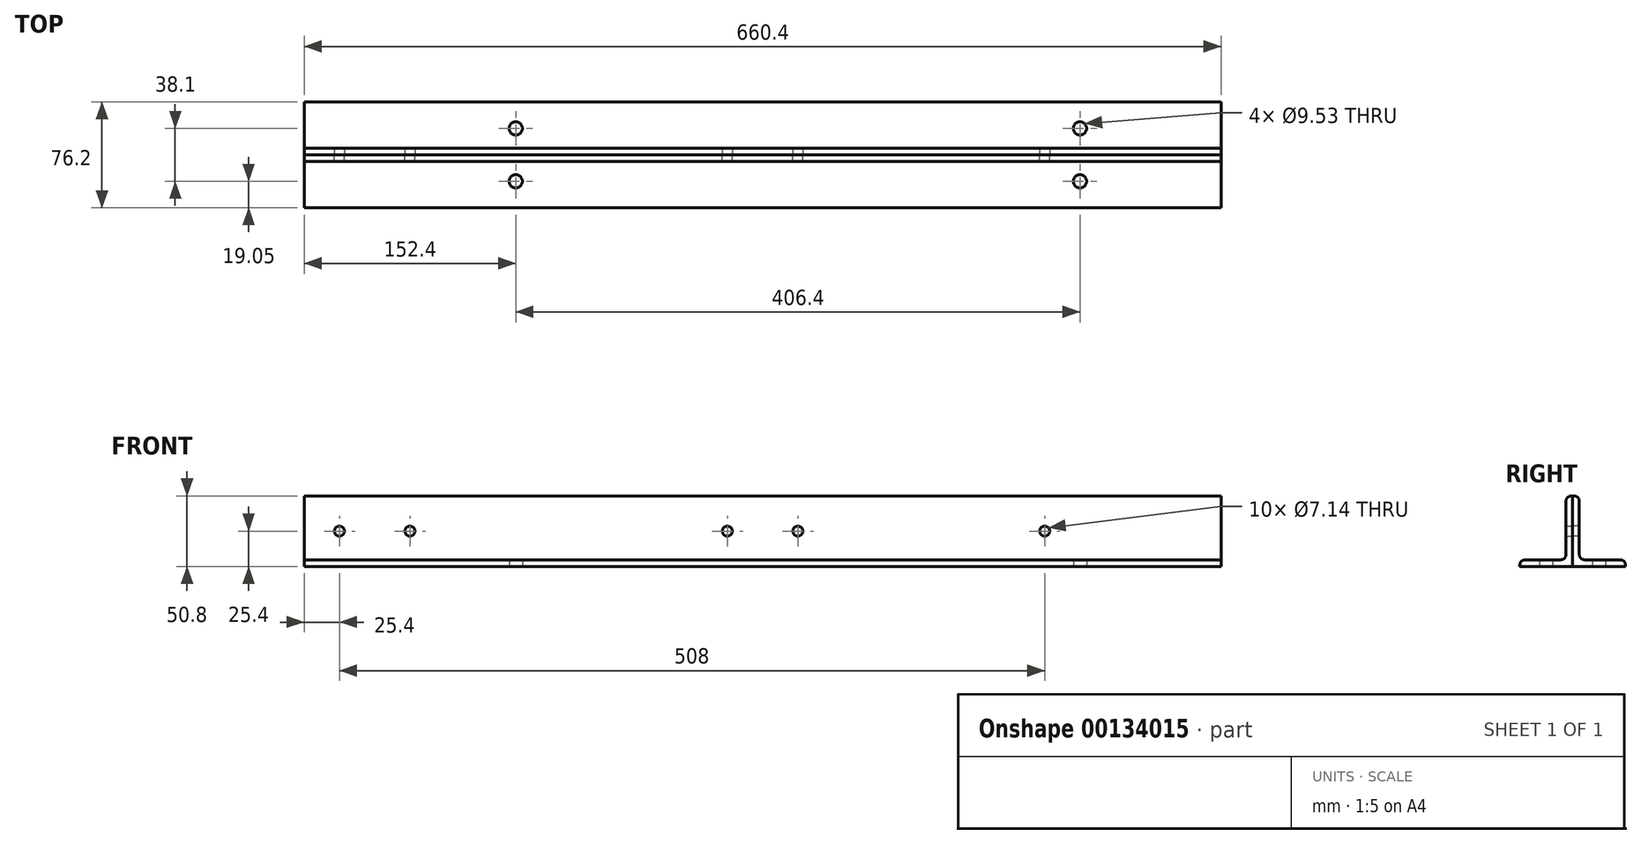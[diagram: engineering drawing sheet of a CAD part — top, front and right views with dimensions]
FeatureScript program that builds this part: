
annotation { "Feature Type Name" : "Feature", "Feature Type Description" : "" }
export const myFeature = defineFeature(function(context is Context, id is Id, definition is map)
    precondition{}
    {
        {
            var Q0;
            Q0=qCreatedBy(makeId("Right.planeOp"),FACE);
            var sketch = newSketch(context, id + "F0", { "sketchPlane" : qUnion([Q0])});
            skLineSegment(sketch, "E0", {"start": v(0, 50.8) * mm, "end": v(0, 0) * mm});
            skLineSegment(sketch, "E1", {"start": v(0, 0) * mm, "end": v(-38.1, 0) * mm});
            skLineSegment(sketch, "E2", {"start": v(0, 50.8) * mm, "end": v(-0.97, 50.8) * mm});
            skLineSegment(sketch, "E3", {"start": v(-38.1, 0) * mm, "end": v(-38.1, 0.95) * mm});
            skLineSegment(sketch, "E4", {"start": v(-34.3, 4.76) * mm, "end": v(-8.59, 4.76) * mm});
            skLineSegment(sketch, "E5", {"start": v(-4.78, 47) * mm, "end": v(-4.78, 8.57) * mm});
            skArc(sketch, "E6", {"start": v(-38.1, 0.95) * mm, "mid": v(-36.98, 3.65) * mm, "end": v(-34.3, 4.76) * mm});
            skArc(sketch, "E7", {"start": v(-8.59, 4.76) * mm, "mid": v(-5.9, 5.88) * mm, "end": v(-4.78, 8.57) * mm});
            skArc(sketch, "E8", {"start": v(-4.78, 47) * mm, "mid": v(-3.66, 49.68) * mm, "end": v(-0.97, 50.8) * mm});
            skPoint(sketch, "E9.endSnap0", {"position": v(0, 25.4) * mm});
            skSolve(sketch);
        }
        {
            var Q0;
            Q0 = qSketchRegion(id + "F0", true);
            extrude(context, id + "F1", {"entities" : qUnion([Q0]), "endBound" : BoundingType.SYMMETRIC, "depth" : 660.4 * mm});
        }
        {
            var Q0;
            Q0=makeQuery(id+"F1.opExtrude","SWEPT_FACE",FACE,{"disambiguationData":[OSD([sQuery(id+"F0.wireOp",EDGE,"E0")])]});
            var sketch = newSketch(context, id + "F2", { "sketchPlane" : qUnion([Q0])});
            skLineSegment(sketch, "E10", {"start": v(-203.2, 25.4) * mm, "end": v(254, 25.4) * mm, "construction": true});
            skPoint(sketch, "E11", {"position": v(25.4, 25.4) * mm});
            skLineSegment(sketch, "E12", {"start": v(254, 25.4) * mm, "end": v(304.8, 25.4) * mm, "construction": true});
            skPoint(sketch, "E13", {"position": v(-25.4, 25.4) * mm});
            skSolve(sketch);
        }
        {
            var Q0;
            Q0=sQuery(id+"F2.wireOp",VERTEX,"E10.end");
            var Q1;
            Q1=sQuery(id+"F2.wireOp",VERTEX,"E11");
            var Q2;
            Q2=sQuery(id+"F2.wireOp",VERTEX,"E10.start");
            var Q3;
            Q3=sQuery(id+"F2.wireOp",VERTEX,"E13");
            var Q4;
            Q4=sQuery(id+"F2.wireOp",VERTEX,"E12.end");
            var Q5;
            Q5=makeQuery(id+"F1.opExtrude","SWEPT_BODY",BODY,{"disambiguationData":[OSD([sQuery(id+"F0.wireOp",EDGE,"E0"),sQuery(id+"F0.wireOp",EDGE,"E1"),sQuery(id+"F0.wireOp",EDGE,"E2"),sQuery(id+"F0.wireOp",EDGE,"E3"),sQuery(id+"F0.wireOp",EDGE,"E4"),sQuery(id+"F0.wireOp",EDGE,"E5"),sQuery(id+"F0.wireOp",EDGE,"E6"),sQuery(id+"F0.wireOp",EDGE,"E7"),sQuery(id+"F0.wireOp",EDGE,"E8")])]});
            hole(context, id + "F3", {"style" : HoleStyle.SIMPLE, "endStyle" : HoleEndStyle.THROUGH, "holeDiameter" : 7.14 * mm, "locations" : qUnion([Q0, Q1, Q2, Q3, Q4]), "scope" : qUnion([Q5]), "isTappedThrough" : true});
        }
        {
            var Q0;
            Q0=makeQuery(id+"F1.opExtrude","SWEPT_FACE",FACE,{"disambiguationData":[OSD([sQuery(id+"F0.wireOp",EDGE,"E1")])]});
            var sketch = newSketch(context, id + "F4", { "sketchPlane" : qUnion([Q0])});
            skLineSegment(sketch, "E14", {"start": v(330.2, 19.05) * mm, "end": v(228.6, 19.05) * mm, "construction": true});
            skLineSegment(sketch, "E15", {"start": v(228.6, 19.05) * mm, "end": v(-177.8, 19.05) * mm, "construction": true});
            skSolve(sketch);
        }
        {
            var Q0;
            Q0=sQuery(id+"F4.wireOp",VERTEX,"E15.start");
            var Q1;
            Q1=sQuery(id+"F4.wireOp",VERTEX,"E15.end");
            var Q2;
            Q2=makeQuery(id+"F1.opExtrude","SWEPT_BODY",BODY,{"disambiguationData":[OSD([sQuery(id+"F0.wireOp",EDGE,"E0"),sQuery(id+"F0.wireOp",EDGE,"E1"),sQuery(id+"F0.wireOp",EDGE,"E2"),sQuery(id+"F0.wireOp",EDGE,"E3"),sQuery(id+"F0.wireOp",EDGE,"E4"),sQuery(id+"F0.wireOp",EDGE,"E5"),sQuery(id+"F0.wireOp",EDGE,"E6"),sQuery(id+"F0.wireOp",EDGE,"E7"),sQuery(id+"F0.wireOp",EDGE,"E8")])]});
            hole(context, id + "F5", {"style" : HoleStyle.SIMPLE, "endStyle" : HoleEndStyle.THROUGH, "holeDiameter" : 9.52 * mm, "locations" : qUnion([Q0, Q1]), "scope" : qUnion([Q2]), "isTappedThrough" : true});
        }
        {
            var Q0;
            Q0=makeQuery(id+"F1.opExtrude","SWEPT_BODY",BODY,{"disambiguationData":[OSD([sQuery(id+"F0.wireOp",EDGE,"E0"),sQuery(id+"F0.wireOp",EDGE,"E1"),sQuery(id+"F0.wireOp",EDGE,"E2"),sQuery(id+"F0.wireOp",EDGE,"E3"),sQuery(id+"F0.wireOp",EDGE,"E4"),sQuery(id+"F0.wireOp",EDGE,"E5"),sQuery(id+"F0.wireOp",EDGE,"E6"),sQuery(id+"F0.wireOp",EDGE,"E7"),sQuery(id+"F0.wireOp",EDGE,"E8")])]});
            var Q1;
            Q1=qCreatedBy(makeId("Front.planeOp"),FACE);
            mirror(context, id + "F6", {"entities" : qUnion([Q0]), "mirrorPlane" : qUnion([Q1])});
        }
    });
